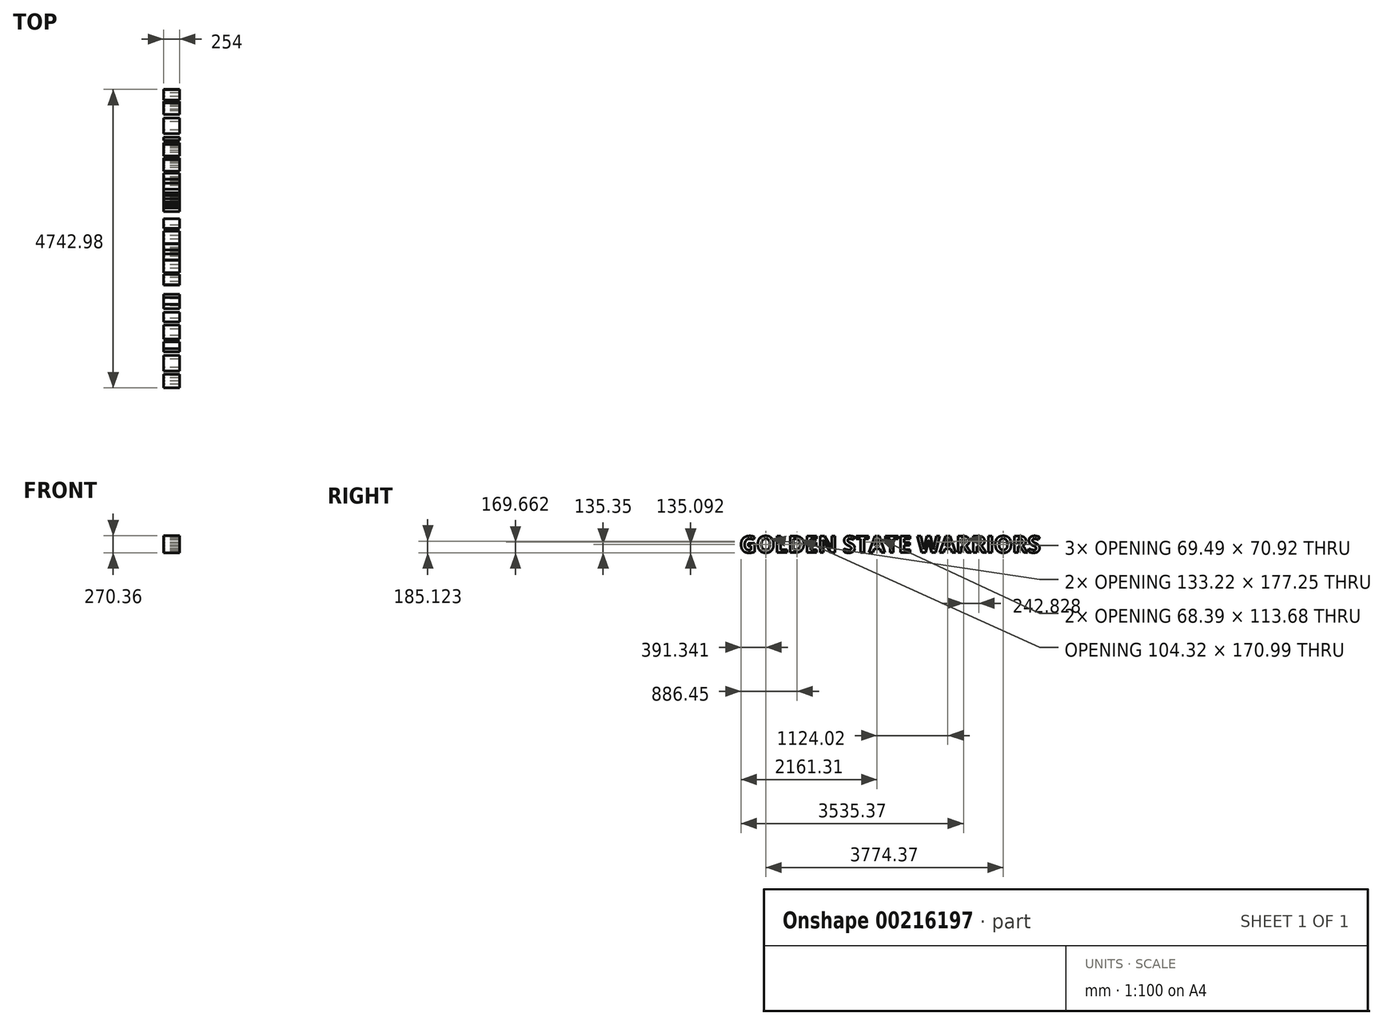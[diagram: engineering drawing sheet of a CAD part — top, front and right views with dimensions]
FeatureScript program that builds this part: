
annotation { "Feature Type Name" : "Feature", "Feature Type Description" : "" }
export const myFeature = defineFeature(function(context is Context, id is Id, definition is map)
    precondition{}
    {
        {
            var Q0;
            Q0=qCreatedBy(makeId("Right.planeOp"),FACE);
            var sketch = newSketch(context, id + "F0", { "sketchPlane" : qUnion([Q0])});
            skText(sketch, "E0", { "text": "GOLDEN STATE WARRIORS", "fontName": "OpenSans-Bold.ttf"});
            const initialGuessF0  = {"E0": [-0.33333, 0, 1, 0, 0.26484]};
            skSetInitialGuess(sketch, initialGuessF0);
            skSolve(sketch);
        }
        {
            var Q0;
            Q0 = qSketchRegion(id + "F0", true);
            extrude(context, id + "F1", {"entities" : qUnion([Q0]), "depth" : 254 * mm});
        }
    });
